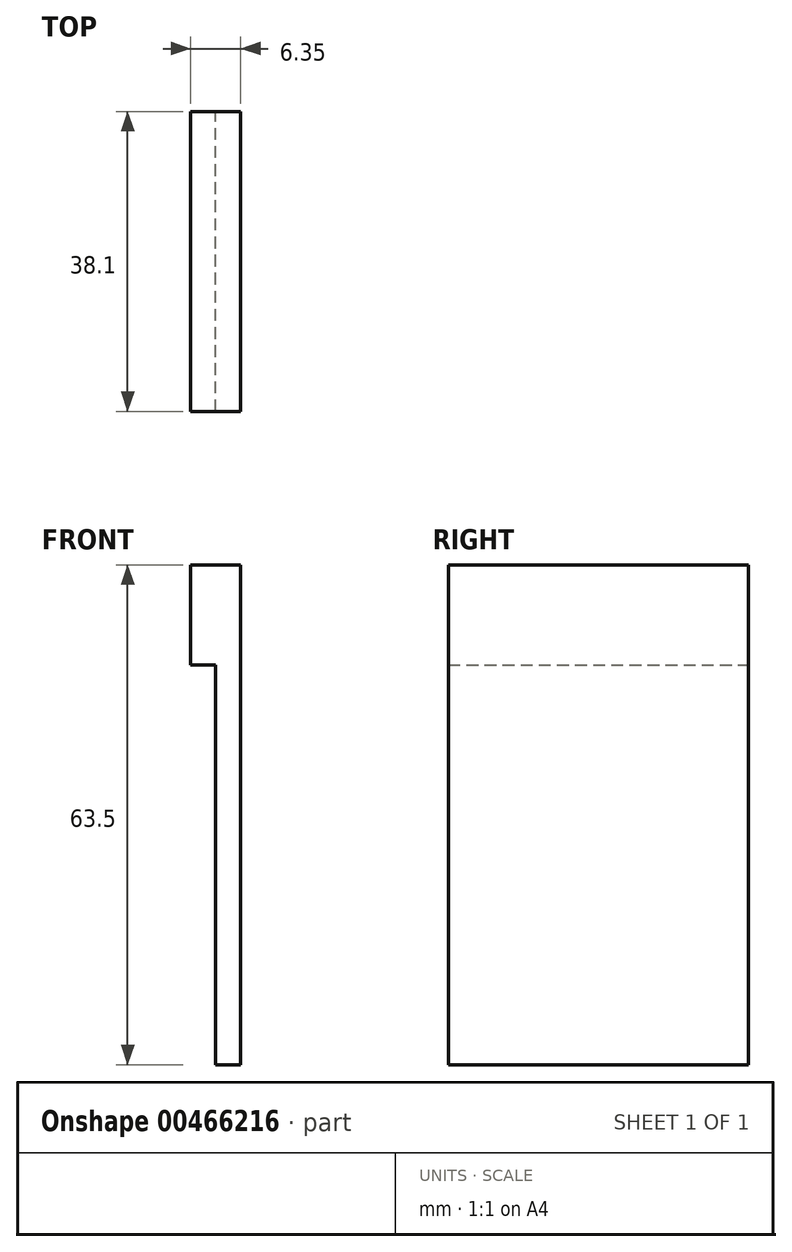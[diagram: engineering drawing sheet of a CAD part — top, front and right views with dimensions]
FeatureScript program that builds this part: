
annotation { "Feature Type Name" : "Feature", "Feature Type Description" : "" }
export const myFeature = defineFeature(function(context is Context, id is Id, definition is map)
    precondition{}
    {
        {
            var Q0;
            Q0=qCreatedBy(makeId("Front.planeOp"),FACE);
            var sketch = newSketch(context, id + "F0", { "sketchPlane" : qUnion([Q0])});
            skLineSegment(sketch, "E0", {"start": v(0, 0) * mm, "end": v(0, 63.5) * mm});
            skLineSegment(sketch, "E1", {"start": v(0, 63.5) * mm, "end": v(-6.35, 63.5) * mm});
            skLineSegment(sketch, "E2", {"start": v(-6.35, 63.5) * mm, "end": v(-6.35, 50.8) * mm});
            skLineSegment(sketch, "E3", {"start": v(-6.35, 50.8) * mm, "end": v(-3.18, 50.8) * mm});
            skLineSegment(sketch, "E4", {"start": v(-3.18, 50.8) * mm, "end": v(-3.18, 0) * mm});
            skLineSegment(sketch, "E5", {"start": v(-3.18, 0) * mm, "end": v(0, 0) * mm});
            skSolve(sketch);
        }
        {
            var Q0;
            Q0 = qSketchRegion(id + "F0", true);
            extrude(context, id + "F1", {"entities" : qUnion([Q0]), "endBound" : BoundingType.SYMMETRIC, "depth" : 38.1 * mm});
        }
    });
